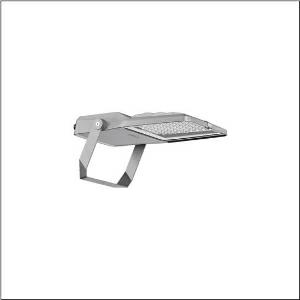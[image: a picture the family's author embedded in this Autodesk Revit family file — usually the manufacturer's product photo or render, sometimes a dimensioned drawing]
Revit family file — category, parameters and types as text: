
# Revit family: floodlight_fl_21_iq_mini___pl61_5xa7772b5c1a_2793
name_source: partatom
category: Lighting Fixtures
units: mm (PartAtom-declared; Revit-internal decimal feet)

## family parameters
Cut with Voids When Loaded = No
Host = Face
Light Source = No
Part Type = Normal
Room Calculation Point = No
Round Connector Dimension = Use Diameter
Shared = No

## types (1)
- --- (1 x LED, 5710 lm, 45.5 W, 4000K)
    Apparent Load = 46 VA
    CIE Flux Codes = 33 65 98 100 100
    Color Rendering = 80
    Color Temperature = 4000K
    Default Elevation = 1800 mm
    Description = Floodlight FL 21 iQ mini, floodlight, primary light control with lens, of PMMA, primary optical cover: protective disc, of toughened safety glass, transparent, light distribution: PL61, light emission: direct distribution, installation type: surface-mounted, LED, High Power LED, rated luminous flux: 5.710lm, luminous efficacy: 126lm/W, light colour: 840, colour temperature: 4000K, control gear: iQ Street-Remote/DALI, control: Street-Remote, Auto-Match, Temp-Guard, Night-Set, Smart-Wire, Desk-Remote (wireless, voltage-free reading and setting of iQ features in the workshop via application-optimized NFC function/RFID function), optimised constant luminous flux control (CLO 2.0), with terminal, 6-pole, mains connection: 220..240V, AC, 50/60Hz, start of lifetime: 46W, end of service life: 48W, reduction: 22W, luminaire housing, of diecast aluminium, powder-coated, Siteco® metallic grey (DB 702S), corrosivity category C5 mid according to DIN EN ISO 12944, suitable for swimming pools, chlorine-resistant, sealing non-destructively replaceable, mounting bracket, of steel, galvanised, powder-coated, Siteco® metallic grey (DB 702S), protection rating (complete): IP66, insulation class (complete): insulation class II (safety insulation), certification: CE, ENEC, VDE, protection symbol: D, impact resistance: IK08, permissible operating ambient temperature: -40..+40°C, permissible operating ambient temperature for outdoor applications: -40..+50°C, standard: DIN EN 12944, LABS conformity tested according to VDMA 24364:2018-05, packaging unit: 1 piece

Light Distribution: PL61
    Height = 70 mm
    Lamp = 1 x LED
    Lamp Light Flux = 5710 lm
    Lamp Power = 45.5 W
    Lamp count = 1
    Length = 485 mm
    Luminous efficacy = 125 lm/W
    Manufacturer = Siteco
    ModVariant = No
    Model = 5XA7772B5C1A
    Number of Poles = 1
    OnlyDefault = Yes
    Power Factor = 1
    Product Name = Floodlight FL 21 iQ mini | PL61
    Product group = floodlight | pylon annexe
    ProductGroupID = 6200
    Protection Class = Protection class II
    Protection Degree = IP 66
    RLX_Detail_Level = 1
    RLX_Emergency_Light_Flux = 0 lm
    RLX_Emergency_Type = 0
    RLX_Emergency_Type_DB = No
    RlxData = <blob elided: 96225 chars, md5=4b1cbd9c>
    Socket = socket
    Standby Power = 0 W
    System Light Flux = 5710 lm
    System Power = 46 W
    Type Comments = factory setting: luminous flux: 100 % | dim-lin: 254 | 463 mA
    Type Image = l_1006845.jpg
    URL = http://relux.com
    VarID = @adj_173404
    Voltage = 0 V
    Weight = 0.00 kg
    Width = 337 mm

## geometry (parser evidence)
native form markers: Blend x4, Sweep x13
no freeform markers — native parametric forms only
